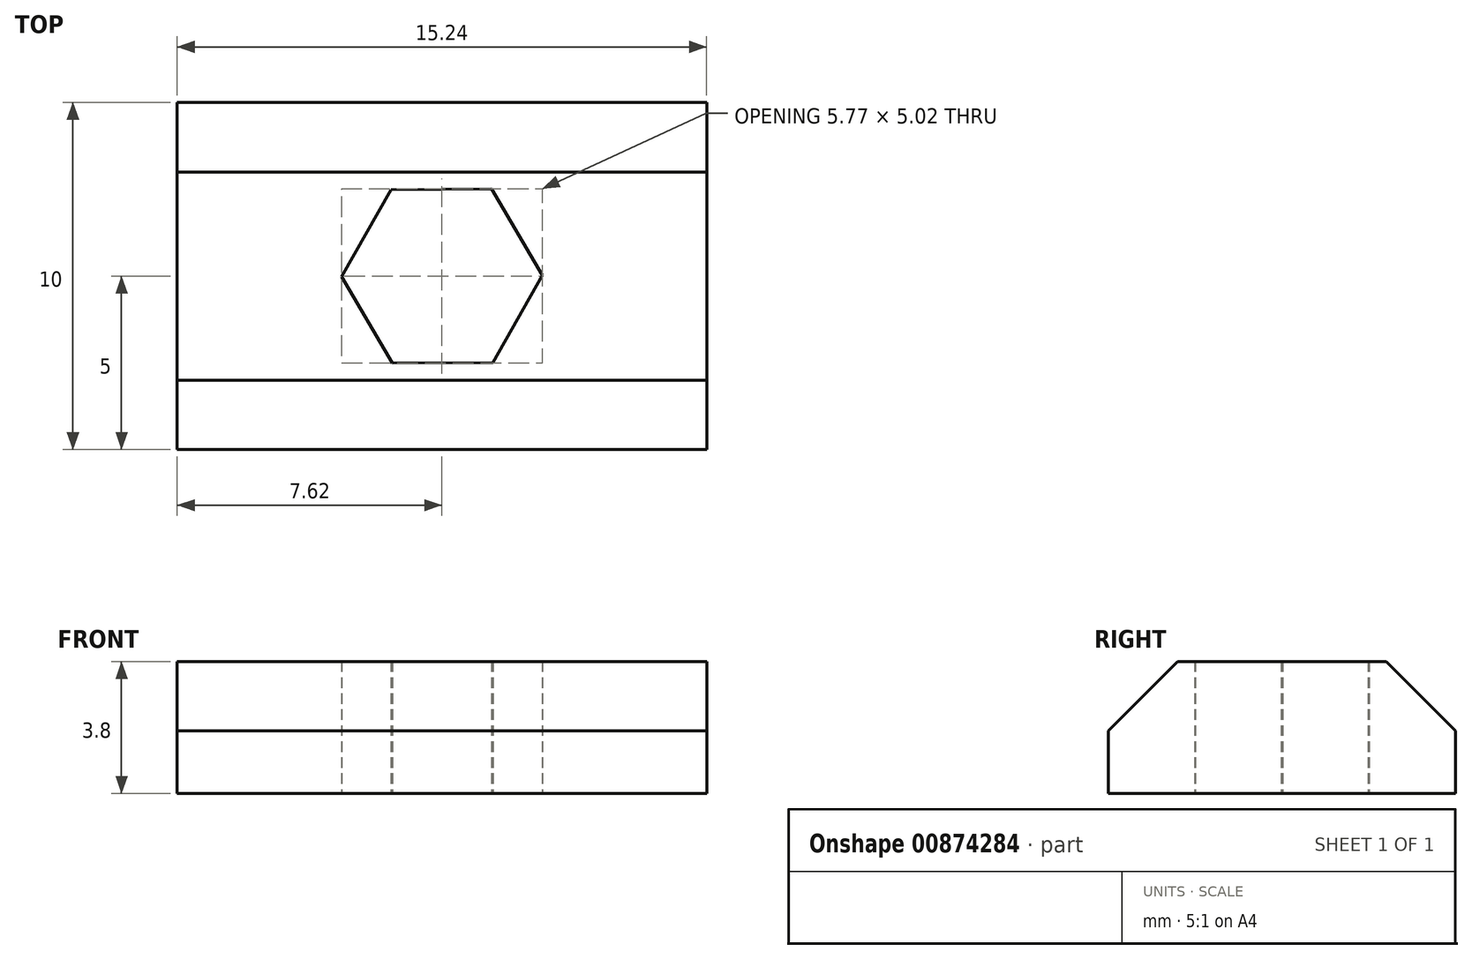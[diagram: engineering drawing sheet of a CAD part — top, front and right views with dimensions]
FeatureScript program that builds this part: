
annotation { "Feature Type Name" : "Feature", "Feature Type Description" : "" }
export const myFeature = defineFeature(function(context is Context, id is Id, definition is map)
    precondition{}
    {
        {
            var Q0;
            Q0=qCreatedBy(makeId("Top.planeOp"),FACE);
            var sketch = newSketch(context, id + "F0", { "sketchPlane" : qUnion([Q0])});
            skLineSegment(sketch, "E0.bottom", {"start": v(7.62, -5) * mm, "end": v(-7.62, -5) * mm});
            skLineSegment(sketch, "E0.top", {"start": v(7.62, 5) * mm, "end": v(-7.62, 5) * mm});
            skLineSegment(sketch, "E0.left", {"start": v(7.62, -5) * mm, "end": v(7.62, 5) * mm});
            skLineSegment(sketch, "E0.right", {"start": v(-7.62, -5) * mm, "end": v(-7.62, 5) * mm});
            skPoint(sketch, "E0.middle", {"position": v(0, 0) * mm});
            skSolve(sketch);
        }
        {
            var Q0;
            Q0=makeQuery(id+"F0.imprint","IMPRINT",FACE,{"disambiguationData":[TD([[makeQuery(id+"F0.imprint","IMPRINT",EDGE,{"derivedFrom":sQuery(id+"F0.wireOp",EDGE,"E0.bottom")}),-1.0]])]});
            extrude(context, id + "F1", {"entities" : qUnion([Q0]), "depth" : 3.8 * mm, "offsetDistance" : 25.4 * mm});
        }
        {
            var Q0;
            Q0=makeQuery(id+"F1.opExtrude","CAP_EDGE",EDGE,{"disambiguationData":[OSD([sQuery(id+"F0.wireOp",EDGE,"E0.bottom")])],"isStart":false});
            var Q1;
            Q1=makeQuery(id+"F1.opExtrude","CAP_EDGE",EDGE,{"disambiguationData":[OSD([sQuery(id+"F0.wireOp",EDGE,"E0.top")])],"isStart":false});
            chamfer(context, id + "F2", {"entities" : qUnion([Q0, Q1]), "chamferType" : ChamferType.OFFSET_ANGLE, "width" : 2 * mm, "oppositeDirection" : false, "angle" : 45 * degree, "tangentPropagation" : true});
        }
        {
            var Q0;
            Q0=makeQuery(id+"F1.opExtrude","CAP_FACE",FACE,{"disambiguationData":[OSD([sQuery(id+"F0.wireOp",EDGE,"E0.bottom"),sQuery(id+"F0.wireOp",EDGE,"E0.top"),sQuery(id+"F0.wireOp",EDGE,"E0.left"),sQuery(id+"F0.wireOp",EDGE,"E0.right")])],"isStart":true});
            var sketch = newSketch(context, id + "F3", { "sketchPlane" : qUnion([Q0])});
            skCircle(sketch, "E1.cCircle", {"center": v(0, 0) * mm, "radius": 2.5 * mm, "construction": true});
            skLineSegment(sketch, "E1.0", {"start": v(2.89, -0.02) * mm, "end": v(1.42, -2.51) * mm});
            skLineSegment(sketch, "E1.1", {"start": v(1.42, -2.51) * mm, "end": v(-1.46, -2.49) * mm});
            skLineSegment(sketch, "E1.2", {"start": v(-1.46, -2.49) * mm, "end": v(-2.89, 0.02) * mm});
            skLineSegment(sketch, "E1.3", {"start": v(-2.89, 0.02) * mm, "end": v(-1.42, 2.51) * mm});
            skLineSegment(sketch, "E1.4", {"start": v(-1.42, 2.51) * mm, "end": v(1.46, 2.49) * mm});
            skLineSegment(sketch, "E1.5", {"start": v(1.46, 2.49) * mm, "end": v(2.89, -0.02) * mm});
            skPoint(sketch, "E1.0.midPoint", {"position": v(2.16, -1.27) * mm});
            skSolve(sketch);
        }
        {
            var Q0;
            Q0=makeQuery(id+"F3.imprint","IMPRINT",FACE,{"disambiguationData":[TD([[makeQuery(id+"F3.imprint","IMPRINT",EDGE,{"derivedFrom":sQuery(id+"F3.wireOp",EDGE,"E1.0")}),-1.0]])]});
            extrude(context, id + "F4", {"entities" : qUnion([Q0]), "operationType" : NewBodyOperationType.REMOVE, "oppositeDirection" : true, "depth" : 4 * mm, "offsetDistance" : 25 * mm});
        }
    });
